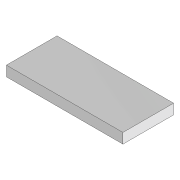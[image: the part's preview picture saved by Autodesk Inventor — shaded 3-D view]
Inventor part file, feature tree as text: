
AUTODESK INVENTOR PART (.ipt)
format: ipt  version: 2022.5 (Build 265521000, 521)  size: 83,968 bytes
history: native  units: mm
features: reference x7, other x7, extrude x2, sketch x1
ambient origin geometry x8: Origin, YZ Plane, XZ Plane, XY Plane, X Axis, Y Axis, Z Axis, Center Point
bodies: Solid1 (feature_tree)
feature tree (17):
  extrude  "Extrusion1"  Depth=40.0mm
  extrude  "Extrusion2"  Depth=92.0mm
  sketch  "Sketch2"  dims[d2=8.0mm d3=0.0mm d7=40.0mm d8=92.0mm d9=0.0mm d10=0.0mm]
  reference  "Reference1"
  reference  "Reference2"
  reference  "Reference3"
  reference  "Reference4"
  reference  "Reference5"
  reference  "Reference6"
  reference  "Reference7"
  parser-record x1  (decoder bookkeeping rows leaked as tree rows — omitted from the tree; the rows remain in map.json)
  other  "AssemblyFrame.iam"
  other  "Motor1x40:2"
  other  "MotorBase:1"
  other  "Motor1x40:1"
  other  "MotorBase:2"
  other  "Nut3:2"
note: 1 file-system path scrubbed to <path> (originals preserved in map.json)
